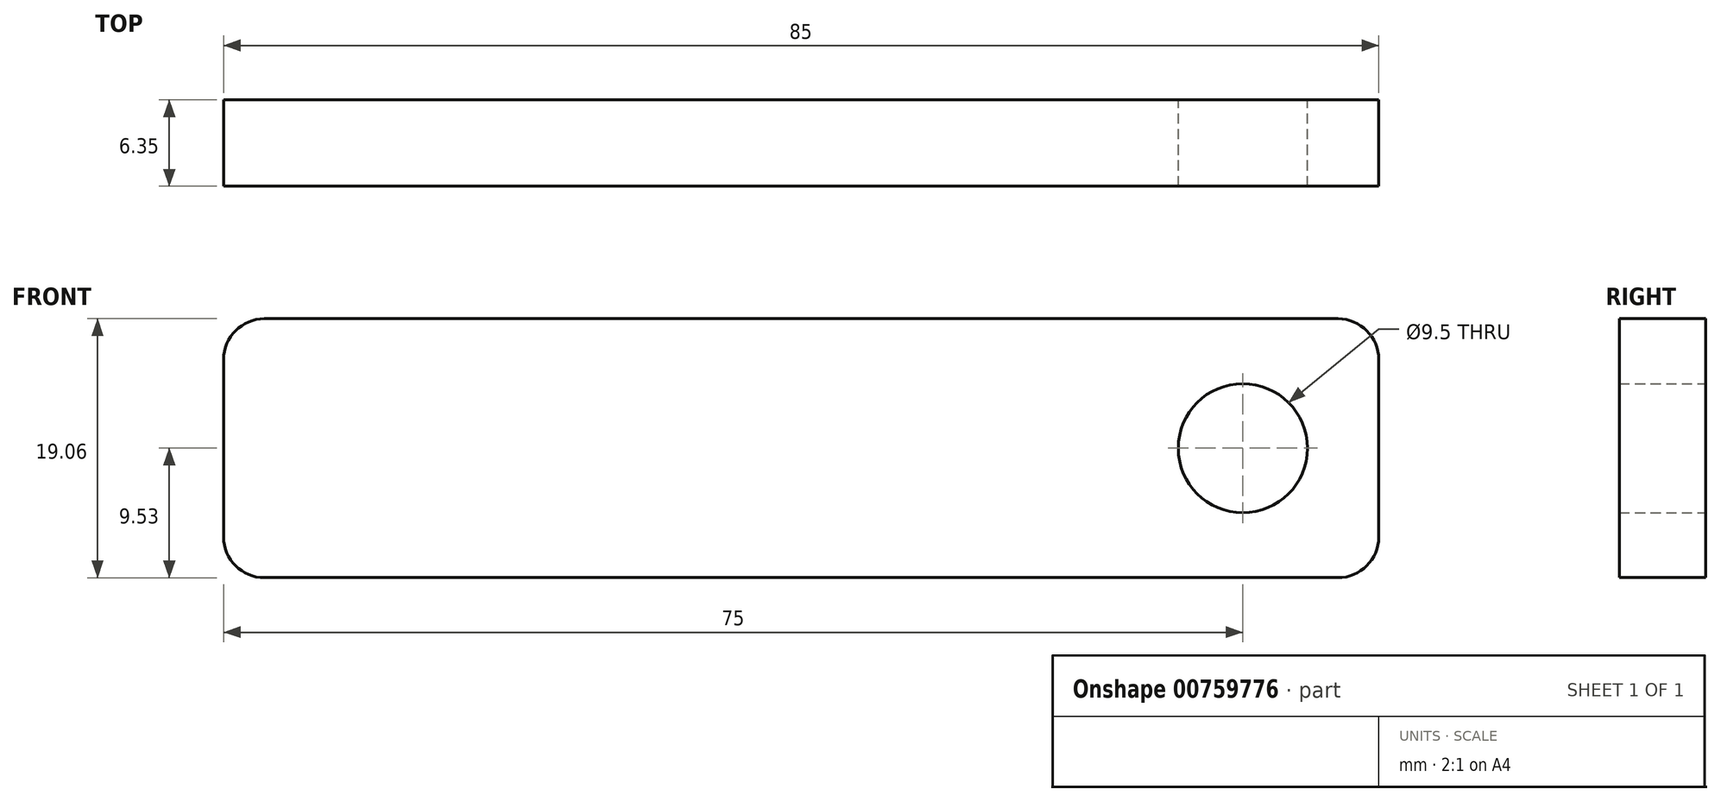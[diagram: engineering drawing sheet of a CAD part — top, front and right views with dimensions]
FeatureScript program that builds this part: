
annotation { "Feature Type Name" : "Feature", "Feature Type Description" : "" }
export const myFeature = defineFeature(function(context is Context, id is Id, definition is map)
    precondition{}
    {
        {
            var Q0;
            Q0=qCreatedBy(makeId("Front.planeOp"),FACE);
            var sketch = newSketch(context, id + "F0", { "sketchPlane" : qUnion([Q0])});
            skLineSegment(sketch, "E0.bottom", {"start": v(-39.5, 9.53) * mm, "end": v(39.5, 9.53) * mm});
            skLineSegment(sketch, "E0.top", {"start": v(-39.5, -9.52) * mm, "end": v(39.5, -9.52) * mm});
            skLineSegment(sketch, "E0.left", {"start": v(-42.5, 6.53) * mm, "end": v(-42.5, -6.52) * mm});
            skLineSegment(sketch, "E0.right", {"start": v(42.5, 6.53) * mm, "end": v(42.5, -6.52) * mm});
            skPoint(sketch, "E0.middle", {"position": v(0, 0) * mm});
            skPoint(sketch, "E1.visualSharp", {"position": v(-42.5, 9.53) * mm});
            skArc(sketch, "E1.filletArc", {"start": v(-39.5, 9.53) * mm, "mid": v(-41.62, 8.65) * mm, "end": v(-42.5, 6.53) * mm});
            skPoint(sketch, "E2.visualSharp", {"position": v(-42.5, -9.52) * mm});
            skArc(sketch, "E2.filletArc", {"start": v(-42.5, -6.52) * mm, "mid": v(-41.62, -8.65) * mm, "end": v(-39.5, -9.52) * mm});
            skPoint(sketch, "E3.visualSharp", {"position": v(42.5, -9.52) * mm});
            skArc(sketch, "E3.filletArc", {"start": v(39.5, -9.52) * mm, "mid": v(41.62, -8.65) * mm, "end": v(42.5, -6.52) * mm});
            skPoint(sketch, "E4.visualSharp", {"position": v(42.5, 9.53) * mm});
            skArc(sketch, "E4.filletArc", {"start": v(42.5, 6.53) * mm, "mid": v(41.62, 8.65) * mm, "end": v(39.5, 9.53) * mm});
            skSolve(sketch);
        }
        {
            var Q0;
            Q0=makeQuery(id+"F0.imprint","IMPRINT",FACE,{"disambiguationData":[TD([[makeQuery(id+"F0.imprint","IMPRINT",EDGE,{"derivedFrom":sQuery(id+"F0.wireOp",EDGE,"E0.bottom")}),-1.0]])]});
            var sketch = newSketch(context, id + "F1", { "sketchPlane" : qUnion([Q0])});
            skCircle(sketch, "E5", {"center": v(32.5, 0) * mm, "radius": 4.75 * mm});
            skSolve(sketch);
        }
        {
            var Q0;
            Q0=makeQuery(id+"F0.imprint","IMPRINT",FACE,{"disambiguationData":[TD([[makeQuery(id+"F0.imprint","IMPRINT",EDGE,{"derivedFrom":sQuery(id+"F0.wireOp",EDGE,"E0.bottom")}),-1.0]])]});
            extrude(context, id + "F2", {"entities" : qUnion([Q0]), "depth" : 6.35 * mm, "offsetDistance" : 25 * mm});
        }
        {
            var Q0;
            Q0=sQuery(id+"F1.wireOp",VERTEX,"E5.center");
            var Q1;
            Q1=makeQuery(id+"F2.opExtrude","SWEPT_BODY",BODY,{"disambiguationData":[OSD([sQuery(id+"F0.wireOp",EDGE,"E0.bottom"),sQuery(id+"F0.wireOp",EDGE,"E0.top"),sQuery(id+"F0.wireOp",EDGE,"E0.left"),sQuery(id+"F0.wireOp",EDGE,"E0.right"),sQuery(id+"F0.wireOp",EDGE,"E1.filletArc"),sQuery(id+"F0.wireOp",EDGE,"E2.filletArc"),sQuery(id+"F0.wireOp",EDGE,"E3.filletArc"),sQuery(id+"F0.wireOp",EDGE,"E4.filletArc")])]});
            hole(context, id + "F3", {"style" : HoleStyle.SIMPLE, "endStyle" : HoleEndStyle.THROUGH, "oppositeDirection" : true, "holeDiameter" : 9.5 * mm, "majorDiameter" : 5 * mm, "isTappedThrough" : true, "tappedDepth" : 12 * mm, "tapClearance" : 3, "locations" : qUnion([Q0]), "scope" : qUnion([Q1])});
        }
    });
